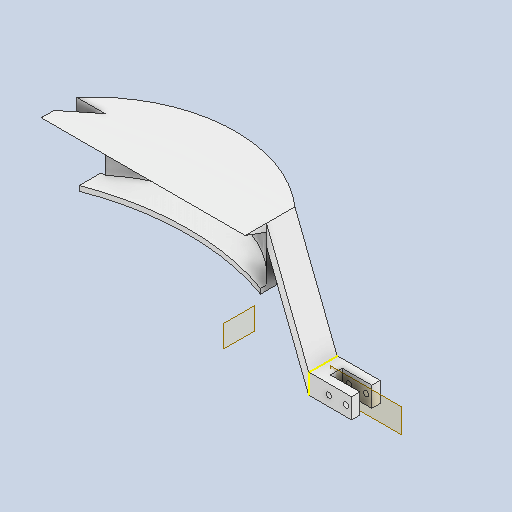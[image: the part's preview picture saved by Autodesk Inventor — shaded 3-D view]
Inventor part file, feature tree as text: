
AUTODESK INVENTOR PART (.ipt)
format: ipt  version: 2024.3 (Build 283343000, 343)  size: 155,648 bytes
history: native  units: mm
features: sketch x5, other x3, plane x2
ambient origin geometry x8: Origin, YZ Plane, XZ Plane, XY Plane, X Axis, Y Axis, Z Axis, Center Point
bodies: Solid1 (feature_tree)
feature tree (10):
  other  "pinzatula1.ipt"
  other  "Solid1::pinzatula1.ipt"
  other  "TaggingFeature1"
  sketch  "Sketch1"  dims[d0=10.0mm]
  sketch  "Sketch2"
  sketch  "Sketch3"
  sketch  "Sketch4"
  sketch  "Sketch5"
  plane  "Work Plane1"
  plane  "Work Plane2"
